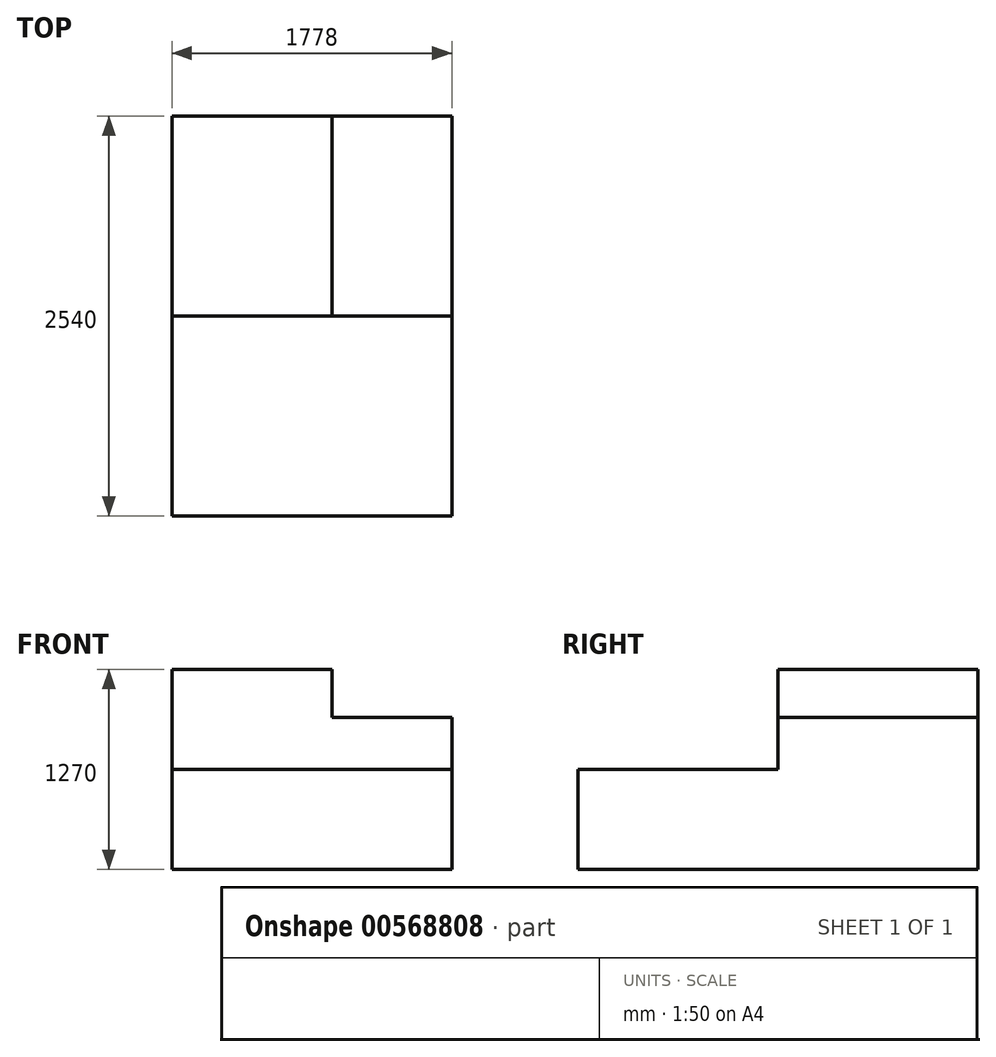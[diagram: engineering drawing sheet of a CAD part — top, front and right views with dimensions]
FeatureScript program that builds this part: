
annotation { "Feature Type Name" : "Feature", "Feature Type Description" : "" }
export const myFeature = defineFeature(function(context is Context, id is Id, definition is map)
    precondition{}
    {
        {
            var Q0;
            Q0=qCreatedBy(makeId("Right.planeOp"),FACE);
            var sketch = newSketch(context, id + "F0", { "sketchPlane" : qUnion([Q0])});
            skLineSegment(sketch, "E0.bottom", {"start": v(0, 0) * mm, "end": v(2540, 0) * mm});
            skLineSegment(sketch, "E0.top", {"start": v(0, 635) * mm, "end": v(2540, 635) * mm});
            skLineSegment(sketch, "E0.left", {"start": v(0, 0) * mm, "end": v(0, 635) * mm});
            skLineSegment(sketch, "E0.right", {"start": v(2540, 0) * mm, "end": v(2540, 635) * mm});
            skSolve(sketch);
        }
        {
            var Q0;
            Q0=makeQuery(id+"F0.imprint","IMPRINT",FACE,{"disambiguationData":[TD([[makeQuery(id+"F0.imprint","IMPRINT",EDGE,{"derivedFrom":sQuery(id+"F0.wireOp",EDGE,"E0.bottom")}),1.0]])]});
            extrude(context, id + "F1", {"entities" : qUnion([Q0]), "depth" : 1778 * mm, "offsetDistance" : 25.4 * mm});
        }
        {
            var Q0;
            Q0=makeQuery(id+"F1.opExtrude","CAP_FACE",FACE,{"disambiguationData":[OSD([sQuery(id+"F0.wireOp",EDGE,"E0.bottom"),sQuery(id+"F0.wireOp",EDGE,"E0.top"),sQuery(id+"F0.wireOp",EDGE,"E0.left"),sQuery(id+"F0.wireOp",EDGE,"E0.right")])],"isStart":false});
            var sketch = newSketch(context, id + "F2", { "sketchPlane" : qUnion([Q0])});
            skLineSegment(sketch, "E1.bottom", {"start": v(2540, 635) * mm, "end": v(1270, 635) * mm});
            skLineSegment(sketch, "E1.top", {"start": v(2540, 965.2) * mm, "end": v(1270, 965.2) * mm});
            skLineSegment(sketch, "E1.left", {"start": v(2540, 635) * mm, "end": v(2540, 965.2) * mm});
            skLineSegment(sketch, "E1.right", {"start": v(1270, 635) * mm, "end": v(1270, 965.2) * mm});
            skSolve(sketch);
        }
        {
            var Q0;
            Q0=makeQuery(id+"F2.imprint","IMPRINT",FACE,{"disambiguationData":[TD([[makeQuery(id+"F2.imprint","IMPRINT",EDGE,{"derivedFrom":sQuery(id+"F2.wireOp",EDGE,"E1.bottom")}),1.0]])]});
            extrude(context, id + "F3", {"entities" : qUnion([Q0]), "operationType" : NewBodyOperationType.ADD, "oppositeDirection" : true, "depth" : 1778 * mm, "offsetDistance" : 25.4 * mm});
        }
        {
            var Q0;
            Q0=makeQuery(id+"F3.boolean.opBoolean","MERGE",FACE,{"derivedFrom":[makeQuery(id+"F1.opExtrude","CAP_FACE",FACE,{"disambiguationData":[OSD([sQuery(id+"F0.wireOp",EDGE,"E0.bottom"),sQuery(id+"F0.wireOp",EDGE,"E0.top"),sQuery(id+"F0.wireOp",EDGE,"E0.left"),sQuery(id+"F0.wireOp",EDGE,"E0.right")])],"isStart":true}),makeQuery(id+"F3.opExtrude","CAP_FACE",FACE,{"disambiguationData":[OSD([sQuery(id+"F2.wireOp",EDGE,"E1.bottom"),sQuery(id+"F2.wireOp",EDGE,"E1.top"),sQuery(id+"F2.wireOp",EDGE,"E1.left"),sQuery(id+"F2.wireOp",EDGE,"E1.right")])],"isStart":false})]});
            var sketch = newSketch(context, id + "F4", { "sketchPlane" : qUnion([Q0])});
            skLineSegment(sketch, "E2.bottom", {"start": v(-2540, 965.2) * mm, "end": v(-1270, 965.2) * mm});
            skLineSegment(sketch, "E2.top", {"start": v(-2540, 1270) * mm, "end": v(-1270, 1270) * mm});
            skLineSegment(sketch, "E2.left", {"start": v(-2540, 965.2) * mm, "end": v(-2540, 1270) * mm});
            skLineSegment(sketch, "E2.right", {"start": v(-1270, 965.2) * mm, "end": v(-1270, 1270) * mm});
            skSolve(sketch);
        }
        {
            var Q0;
            Q0=makeQuery(id+"F4.imprint","IMPRINT",FACE,{"disambiguationData":[TD([[makeQuery(id+"F4.imprint","IMPRINT",EDGE,{"derivedFrom":sQuery(id+"F4.wireOp",EDGE,"E2.bottom")}),1.0]])]});
            extrude(context, id + "F5", {"entities" : qUnion([Q0]), "operationType" : NewBodyOperationType.ADD, "oppositeDirection" : true, "depth" : 1016 * mm, "offsetDistance" : 25.4 * mm});
        }
    });
